# Revit family: 8. Секция пластинчатого рекуператора ANR R1, R3
name_source: partatom
category: Оборудование
revit_build: Autodesk Revit 2016 (Build: 20151209_0715(x64)
units: mm (PartAtom-declared; Revit-internal decimal feet)

## family parameters
Всегда вертикально = Да
На основе рабочей плоскости = Нет
Общий = Нет
При загрузке вырезать с полостями = Нет
Размер круглого соединителя = Использовать диаметр
Тип детали = Нормальный
Точка расчета площади = Нет

## types (12) — shared parameters
h = 180 мм
Единица измерения = шт.
Завод изготовитель = KORF
Ключевая пометка = Вентиляция
Раздел = ОВ
Синий = Синий
высота ножек = 170 мм
значок = Да

## per-type parameters (varying)
| type | А | А1 | Б | Б1 | Высота | Д | Д патрубков | Д1 | Ж | З | Заправочный объем, л | И | И1 | К | К1 | К2 | К5 | Материал | Наименование и тех.хар-ка | Середина | Ширина |
| ANR 20 R1 | 1660 мм | 1640 мм | 3273 мм | 3253 мм | 3198 мм | 3725 мм | 28 мм | 3705 мм | 813 мм | 532 мм | 7 м³ | 473 мм | 236 мм | 778 мм | 1556 мм | 593 мм | 1074 мм | Сталь серая | Секция пластинчатого рекуператора со встречным дви-
жением потоков приточного
и вытяжного воздуха | 1807 мм | 1585 мм |
| ANR 25 R1 | 2045 мм | 2025 мм | 4043 мм | 4023 мм | 3968 мм | 3725 мм | 28 мм | 3705 мм | 1006 мм | 532 мм | 37.8 м³ | 473 мм | 236 мм | 778 мм | 1556 мм | 593 мм | 1074 мм | Сталь серая | Секция пластинчатого рекуператора со встречным дви-
жением потоков приточного
и вытяжного воздуха | 2192 мм | 1970 мм |
| ANR 7 R1 | 1100 мм | 1080 мм | 2593 мм | 2573 мм | 2518 мм | 2150 мм | 40 мм | 2130 мм | 643 мм | 307 мм | 14.3 м³ | 763 мм | 382 мм | 447 мм | 895 мм | 341 мм | 618 мм | Сталь серая | Секция пластинчатого рекуператора со встречным дви-
жением потоков приточного
и вытяжного воздуха | 1467 мм | 1025 мм |
| ANR 8 R1 | 1320 мм | 1300 мм | 2593 мм | 2573 мм | 2518 мм | 2150 мм | 40 мм | 2130 мм | 643 мм | 307 мм | 19.3 м³ | 473 мм | 236 мм | 447 мм | 895 мм | 341 мм | 618 мм | Сталь серая | Секция пластинчатого рекуператора со встречным дви-
жением потоков приточного
и вытяжного воздуха | 1467 мм | 1245 мм |
| ANR 6 R1 | 1100 мм | 1080 мм | 2153 мм | 2133 мм | 2078 мм | 1625 мм | 28 мм | 1605 мм | 533 мм | 232 мм | 7 м³ | 473 мм | 236 мм | 337 мм | 674 мм | 257 мм | 465 мм | Сталь серая | Секция пластинчатого рекуператора со встречным дви-
жением потоков приточного
и вытяжного воздуха | 1247 мм | 1025 мм |
| ANR 12 R1 | 1435 мм | 1415 мм | 2823 мм | 2803 мм | 2748 мм | 2675 мм | 35 мм | 2655 мм | 701 мм | 382 мм | 13.3 м³ | 473 мм | 236 мм | 558 мм | 1115 мм | 425 мм | 770 мм | Сталь серая | Секция пластинчатого рекуператора со встречным дви-
жением потоков приточного
и вытяжного воздуха | 1582 мм | 1360 мм |
| ANR 6 R3 | 1100 мм | 1080 мм | 2153 мм | 2133 мм | 2078 мм | 1625 мм | 28 мм | 1605 мм | 533 мм | 232 мм | 7 м³ | 473 мм | 236 мм | 337 мм | 674 мм | 257 мм | 465 мм | Сталь серая | Секция пластинчатого рекуператора с однонаправленным
движением потоков приточного
и вытяжного воздуха | 1247 мм | 1025 мм |
| ANR 7 R3 | 1100 мм | 1080 мм | 2593 мм | 2573 мм | 2518 мм | 2150 мм | 40 мм | 2130 мм | 643 мм | 307 мм | 14.3 м³ | 763 мм | 382 мм | 447 мм | 895 мм | 341 мм | 618 мм | Сталь серая | Секция пластинчатого рекуператора с однонаправленным | 1467 мм | 1025 мм |
| ANR 8 R3 | 1320 мм | 1300 мм | 2593 мм | 2573 мм | 2518 мм | 2150 мм | 40 мм | 2130 мм | 643 мм | 307 мм | 19.3 м³ | 473 мм | 236 мм | 447 мм | 895 мм | 341 мм | 618 мм | RAL 0000 Серый металл | Секция пластинчатого рекуператора с однонаправленным | 1467 мм | 1245 мм |
| ANR 12 R3 | 1435 мм | 1415 мм | 2823 мм | 2803 мм | 2748 мм | 2675 мм | 35 мм | 2655 мм | 701 мм | 382 мм | 13.3 м³ | 473 мм | 236 мм | 558 мм | 1115 мм | 425 мм | 770 мм | Сталь серая | Секция пластинчатого рекуператора с однонаправленным | 1582 мм | 1360 мм |
| ANR 20 R3 | 1660 мм | 1640 мм | 3273 мм | 3253 мм | 3198 мм | 3725 мм | 28 мм | 3705 мм | 813 мм | 532 мм | 7 м³ | 473 мм | 236 мм | 778 мм | 1556 мм | 593 мм | 1074 мм | Сталь серая | Секция пластинчатого рекуператора с однонаправленным | 1807 мм | 1585 мм |
| ANR 25 R3 | 2045 мм | 2025 мм | 4043 мм | 4023 мм | 3968 мм | 3725 мм | 28 мм | 3705 мм | 1006 мм | 532 мм | 37.8 м³ | 473 мм | 236 мм | 778 мм | 1556 мм | 593 мм | 1074 мм | Сталь серая | Секция пластинчатого рекуператора с однонаправленным | 2192 мм | 1970 мм |

note: column(s) folded — value = type name in every type: Тип, марка, обозначение
